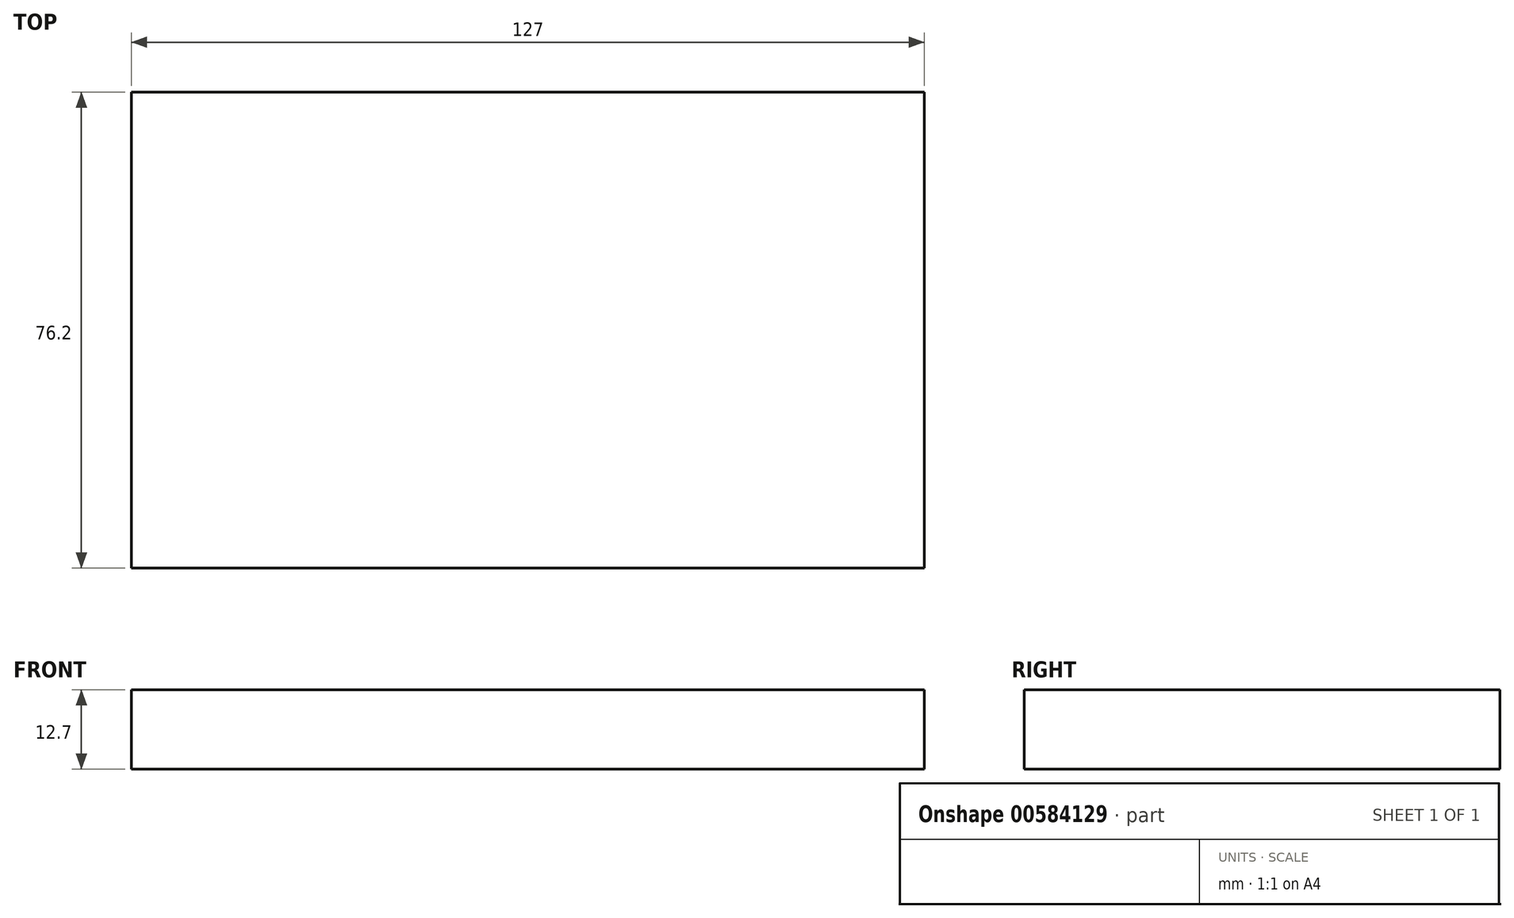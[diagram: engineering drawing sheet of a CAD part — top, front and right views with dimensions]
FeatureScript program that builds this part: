
annotation { "Feature Type Name" : "Feature", "Feature Type Description" : "" }
export const myFeature = defineFeature(function(context is Context, id is Id, definition is map)
    precondition{}
    {
        {
            var Q0;
            Q0=qCreatedBy(makeId("Top.planeOp"),FACE);
            var sketch = newSketch(context, id + "F0", { "sketchPlane" : qUnion([Q0])});
            skLineSegment(sketch, "E0", {"start": v(-62.92, 11.73) * mm, "end": v(-62.92, -64.47) * mm});
            skLineSegment(sketch, "E1", {"start": v(-62.92, -64.47) * mm, "end": v(64.08, -64.47) * mm});
            skLineSegment(sketch, "E2", {"start": v(64.08, -64.47) * mm, "end": v(64.08, 11.73) * mm});
            skLineSegment(sketch, "E3", {"start": v(-62.92, 11.73) * mm, "end": v(64.08, 11.73) * mm});
            skSolve(sketch);
        }
        {
            var Q0;
            Q0=makeQuery(id+"F0.imprint","IMPRINT",FACE,{"disambiguationData":[TD([[makeQuery(id+"F0.imprint","IMPRINT",EDGE,{"derivedFrom":sQuery(id+"F0.wireOp",EDGE,"E0")}),1.0]])]});
            extrude(context, id + "F1", {"entities" : qUnion([Q0]), "depth" : 12.7 * mm, "offsetDistance" : 25.4 * mm});
        }
    });
